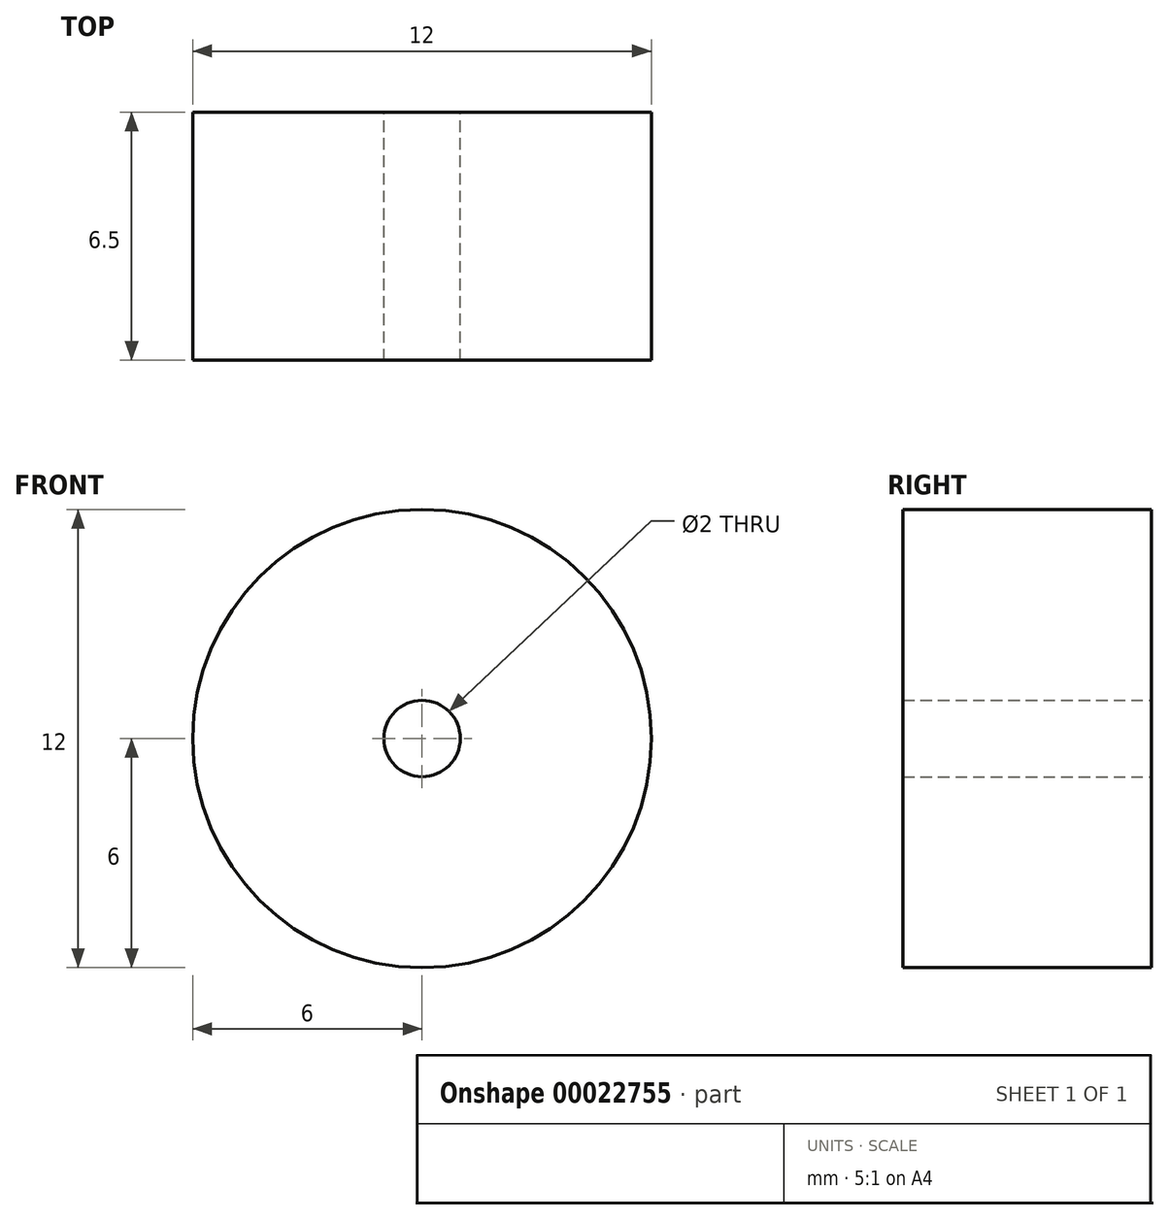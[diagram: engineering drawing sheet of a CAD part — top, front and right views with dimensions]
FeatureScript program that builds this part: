
annotation { "Feature Type Name" : "Feature", "Feature Type Description" : "" }
export const myFeature = defineFeature(function(context is Context, id is Id, definition is map)
    precondition{}
    {
        {
            var Q0;
            Q0=qCreatedBy(makeId("Front.planeOp"),FACE);
            var sketch = newSketch(context, id + "F0", { "sketchPlane" : qUnion([Q0])});
            skCircle(sketch, "E0", {"center": v(0, 0) * mm, "radius": 0.13 * mm});
            skCircle(sketch, "E1", {"center": v(0, 0) * mm, "radius": 6 * mm});
            skCircle(sketch, "E2", {"center": v(0, 0) * mm, "radius": 1 * mm});
            skSolve(sketch);
        }
        {
            var Q0;
            Q0=makeQuery(id+"F0.imprint","IMPRINT",FACE,{"disambiguationData":[TD([[makeQuery(id+"F0.imprint","IMPRINT",EDGE,{"derivedFrom":sQuery(id+"F0.wireOp",EDGE,"E1")}),1.0]])]});
            extrude(context, id + "F1", {"entities" : qUnion([Q0]), "endBound" : BoundingType.SYMMETRIC, "depth" : 6.5 * mm});
        }
    });
